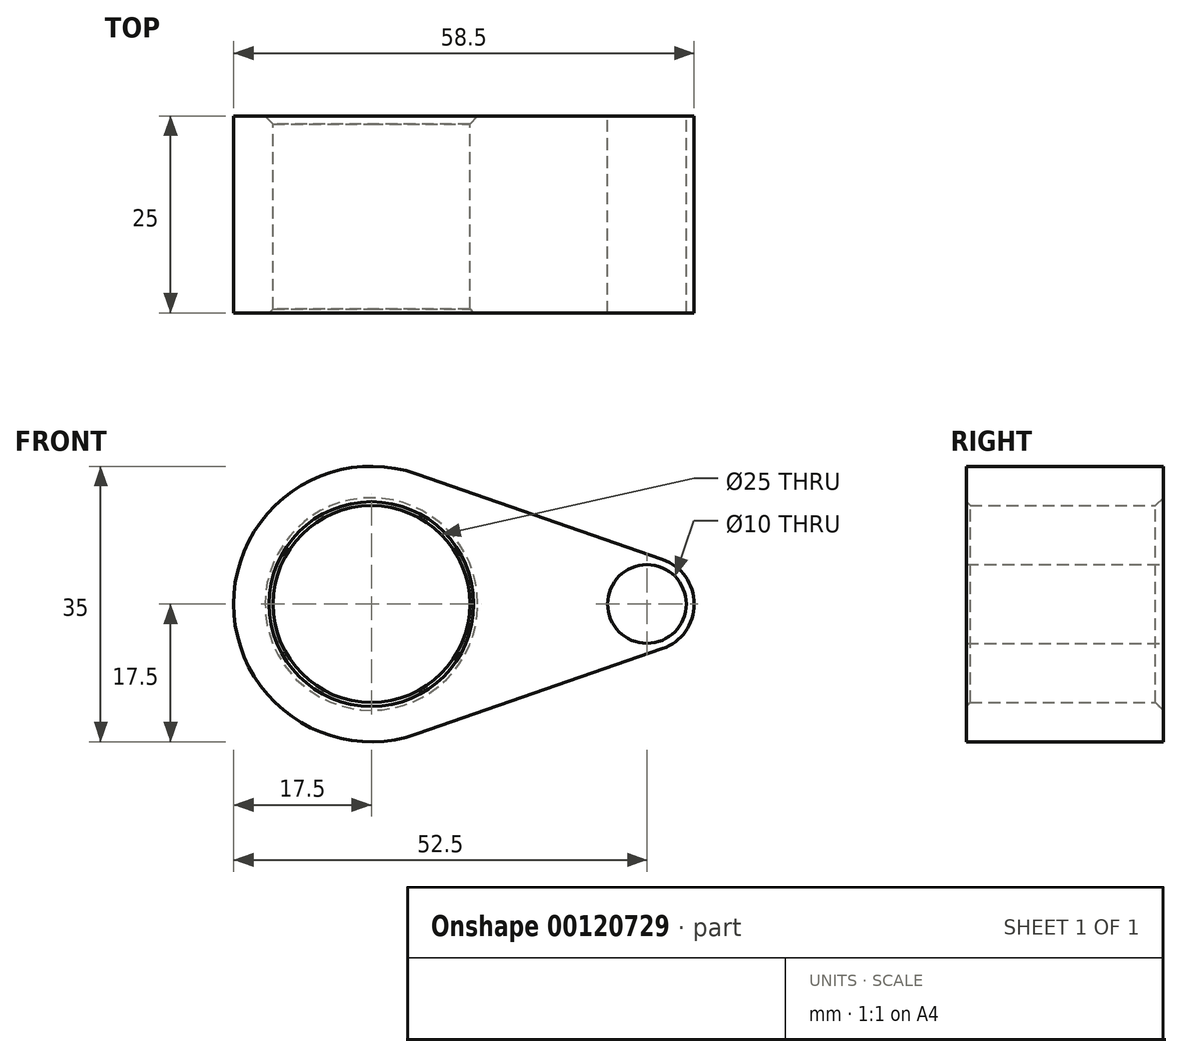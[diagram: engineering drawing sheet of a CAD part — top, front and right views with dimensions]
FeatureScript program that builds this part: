
annotation { "Feature Type Name" : "Feature", "Feature Type Description" : "" }
export const myFeature = defineFeature(function(context is Context, id is Id, definition is map)
    precondition{}
    {
        {
            var Q0;
            Q0=qCreatedBy(makeId("Front.planeOp"),FACE);
            var sketch = newSketch(context, id + "F0", { "sketchPlane" : qUnion([Q0])});
            skCircle(sketch, "E0", {"center": v(0, 0) * mm, "radius": 17.5 * mm});
            skCircle(sketch, "E1", {"center": v(35, 0) * mm, "radius": 6 * mm});
            skLineSegment(sketch, "E2", {"start": v(5.75, 16.53) * mm, "end": v(36.97, 5.67) * mm});
            skLineSegment(sketch, "E3", {"start": v(5.75, -16.53) * mm, "end": v(36.97, -5.67) * mm});
            skCircle(sketch, "E4", {"center": v(0, 0) * mm, "radius": 12.5 * mm});
            skCircle(sketch, "E5", {"center": v(35, 0) * mm, "radius": 5 * mm});
            skSolve(sketch);
        }
        {
            var Q0;
            Q0=makeQuery(id+"F0.imprint","IMPRINT",FACE,{"disambiguationData":[TD([[makeQuery(id+"F0.imprint","IMPRINT",EDGE,{"derivedFrom":sQuery(id+"F0.wireOp",EDGE,"E4")}),-1.0]])]});
            var Q1;
            {var subQ0=sQuery(id+"F0.wireOp",EDGE,"E2");Q1=makeQuery(id+"F0.imprint","IMPRINT",FACE,{"disambiguationData":[TD([[makeQuery(id+"F0.imprint","IMPRINT",EDGE,{"derivedFrom":subQ0}),-1.0]])]});}
            var Q2;
            Q2=makeQuery(id+"F0.imprint","IMPRINT",FACE,{"disambiguationData":[TD([[makeQuery(id+"F0.imprint","IMPRINT",EDGE,{"derivedFrom":sQuery(id+"F0.wireOp",EDGE,"E5")}),-1.0]])]});
            extrude(context, id + "F3", {"entities" : qUnion([Q0, Q1, Q2]), "depth" : 25 * mm});
        }
        {
            var Q0;
            Q0=makeQuery(id+"F3.opExtrude","CAP_EDGE",EDGE,{"disambiguationData":[OSD([sQuery(id+"F0.wireOp",EDGE,"E4")])],"isStart":false});
            chamfer(context, id + "F1", {"entities" : qUnion([Q0]), "width" : 0.5 * mm, "tangentPropagation" : true});
        }
        {
            var Q0;
            Q0=makeQuery(id+"F3.opExtrude","CAP_EDGE",EDGE,{"disambiguationData":[OSD([sQuery(id+"F0.wireOp",EDGE,"E4")])],"isStart":true});
            chamfer(context, id + "F2", {"entities" : qUnion([Q0]), "width" : 1 * mm, "tangentPropagation" : true});
        }
    });
